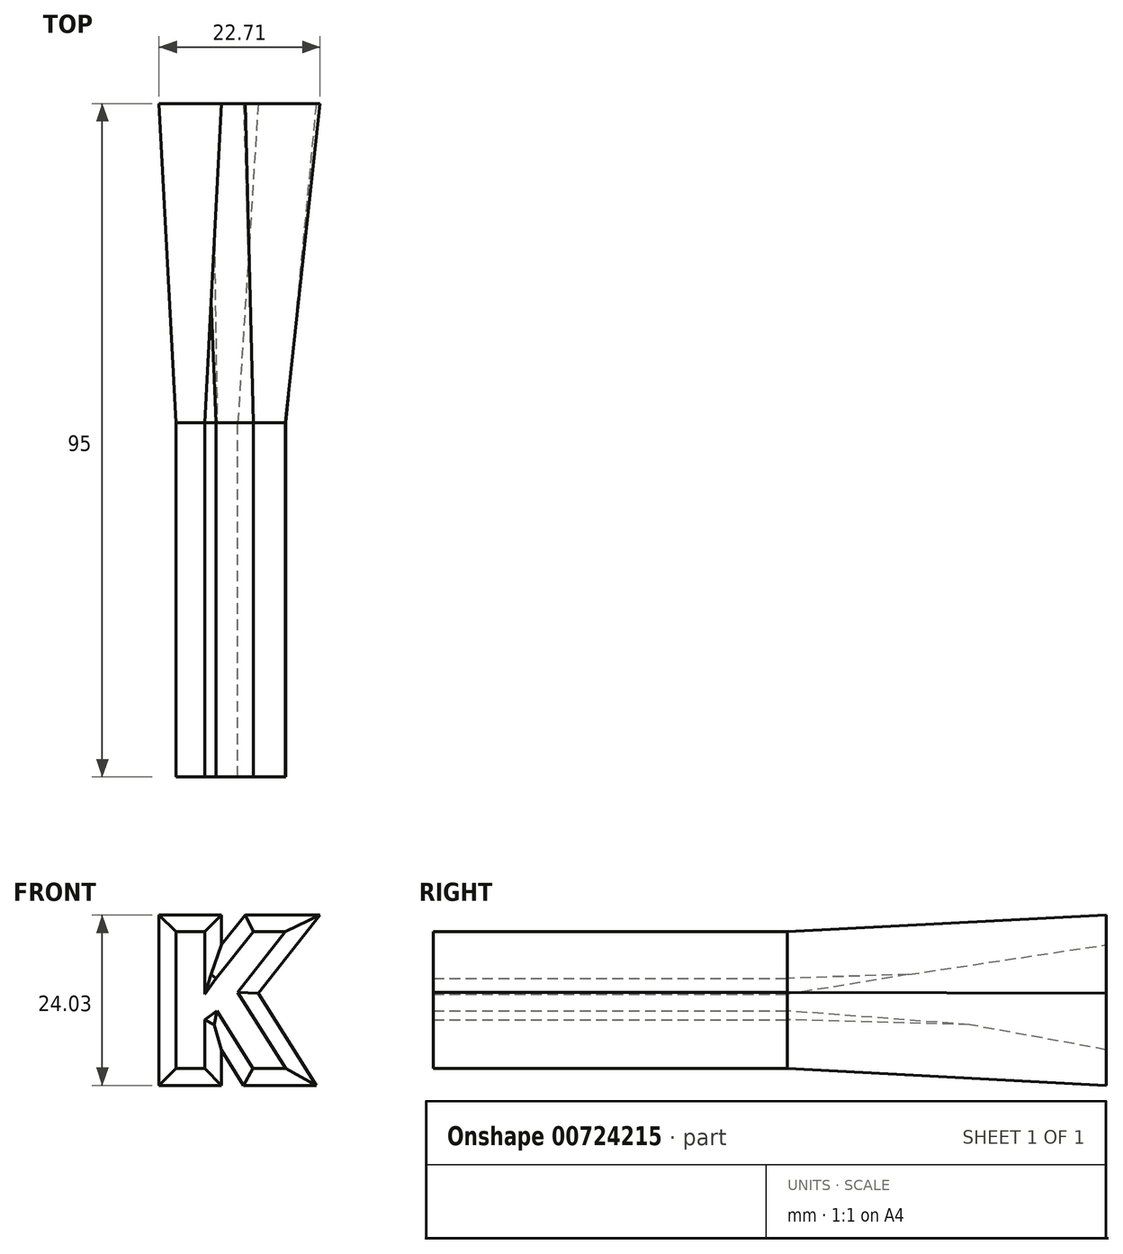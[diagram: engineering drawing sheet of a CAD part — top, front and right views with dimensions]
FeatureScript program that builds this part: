
annotation { "Feature Type Name" : "Feature", "Feature Type Description" : "" }
export const myFeature = defineFeature(function(context is Context, id is Id, definition is map)
    precondition{}
    {
        {
            var Q0;
            Q0=qCreatedBy(makeId("Front.planeOp"),FACE);
            var sketch = newSketch(context, id + "F0", { "sketchPlane" : qUnion([Q0])});
            skCircle(sketch, "E0", {"center": v(5.85, -38.98) * mm, "radius": 53.72 * mm});
            skCircle(sketch, "E1", {"center": v(5.85, -38.98) * mm, "radius": 58.67 * mm, "construction": true});
            skCircle(sketch, "E2", {"center": v(5.85, -38.98) * mm, "radius": 63.5 * mm, "construction": true});
            skLineSegment(sketch, "E3", {"start": v(5.85, -38.98) * mm, "end": v(5.85, 36.33) * mm, "construction": true});
            skLineSegment(sketch, "E4", {"start": v(5.85, -38.98) * mm, "end": v(0.92, 36.33) * mm, "construction": true});
            skLineSegment(sketch, "E5", {"start": v(5.85, 19.7) * mm, "end": v(-60.18, 19.7) * mm, "construction": true});
            skLineSegment(sketch, "E6", {"start": v(5.85, 19.7) * mm, "end": v(-52.99, -1.72) * mm, "construction": true});
            skCircle(sketch, "E7", {"center": v(5.85, -38.98) * mm, "radius": 55.14 * mm, "construction": true});
            skCircle(sketch, "E8", {"center": v(5.85, 19.7) * mm, "radius": 14.6 * mm, "construction": true});
            skCircle(sketch, "E9", {"center": v(-7.87, 14.7) * mm, "radius": 14.6 * mm, "construction": true});
            skArc(sketch, "E10", {"start": v(5.85, 19.7) * mm, "mid": v(4.64, 22.21) * mm, "end": v(3, 24.46) * mm});
            skArc(sketch, "E11", {"start": v(6.66, 16.15) * mm, "mid": v(6.37, 17.95) * mm, "end": v(5.85, 19.7) * mm});
            skArc(sketch, "E12", {"start": v(6.73, 14.74) * mm, "mid": v(6.71, 15.45) * mm, "end": v(6.66, 16.15) * mm});
            skArc(sketch, "E13.MirrorCS", {"start": v(-1.8, 19.2) * mm, "mid": v(-0.94, 21.85) * mm, "end": v(0.4, 24.3) * mm});
            skArc(sketch, "E14.MirrorCS", {"start": v(-2.15, 15.58) * mm, "mid": v(-2.1, 17.4) * mm, "end": v(-1.8, 19.2) * mm});
            skArc(sketch, "E15", {"start": v(3, 24.46) * mm, "mid": v(1.66, 25) * mm, "end": v(0.4, 24.3) * mm});
            skArc(sketch, "E16.MirrorCS", {"start": v(-2.03, 14.16) * mm, "mid": v(-2.1, 14.87) * mm, "end": v(-2.15, 15.58) * mm});
            skCircle(sketch, "E17", {"center": v(5.85, -38.98) * mm, "radius": 26.67 * mm});
            skText(sketch, "E18", { "text": "K", "fontName": "OpenSans-Bold.ttf"});
            const initialGuessF0  = {"E18": [-0.00399, -0.04743, 1, 0, 0.01948]};
            skSetInitialGuess(sketch, initialGuessF0);
            skSolve(sketch);
        }
        {
            var Q0;
            Q0=makeQuery(id+"F0.imprint","IMPRINT",FACE,{"disambiguationData":[TD([[makeQuery(id+"F0.imprint","IMPRINT",EDGE,{"derivedFrom":sQuery(id+"F0.wireOp",EDGE,"E18.sketch_text.stroke-0")}),-1.0]])]});
            extrude(context, id + "F1", {"entities" : qUnion([Q0]), "depth" : 50 * mm, "offsetDistance" : 25 * mm});
        }
        {
            var Q0;
            Q0=makeQuery(id+"F1.opExtrude","CAP_FACE",FACE,{"disambiguationData":[OSD([sQuery(id+"F0.wireOp",EDGE,"E18.sketch_text.stroke-0"),sQuery(id+"F0.wireOp",EDGE,"E18.sketch_text.stroke-1"),sQuery(id+"F0.wireOp",EDGE,"E18.sketch_text.stroke-2"),sQuery(id+"F0.wireOp",EDGE,"E18.sketch_text.stroke-3"),sQuery(id+"F0.wireOp",EDGE,"E18.sketch_text.stroke-4"),sQuery(id+"F0.wireOp",EDGE,"E18.sketch_text.stroke-5"),sQuery(id+"F0.wireOp",EDGE,"E18.sketch_text.stroke-6"),sQuery(id+"F0.wireOp",EDGE,"E18.sketch_text.stroke-7"),sQuery(id+"F0.wireOp",EDGE,"E18.sketch_text.stroke-8"),sQuery(id+"F0.wireOp",EDGE,"E18.sketch_text.stroke-9"),sQuery(id+"F0.wireOp",EDGE,"E18.sketch_text.stroke-10"),sQuery(id+"F0.wireOp",EDGE,"E18.sketch_text.stroke-11"),sQuery(id+"F0.wireOp",EDGE,"E18.sketch_text.stroke-12")])],"isStart":true});
            extrude(context, id + "F2", {"entities" : qUnion([Q0]), "operationType" : NewBodyOperationType.ADD, "depth" : 45 * mm, "offsetDistance" : 25 * mm, "hasDraft" : true, "draftAngle" : 3 * degree});
        }
    });
